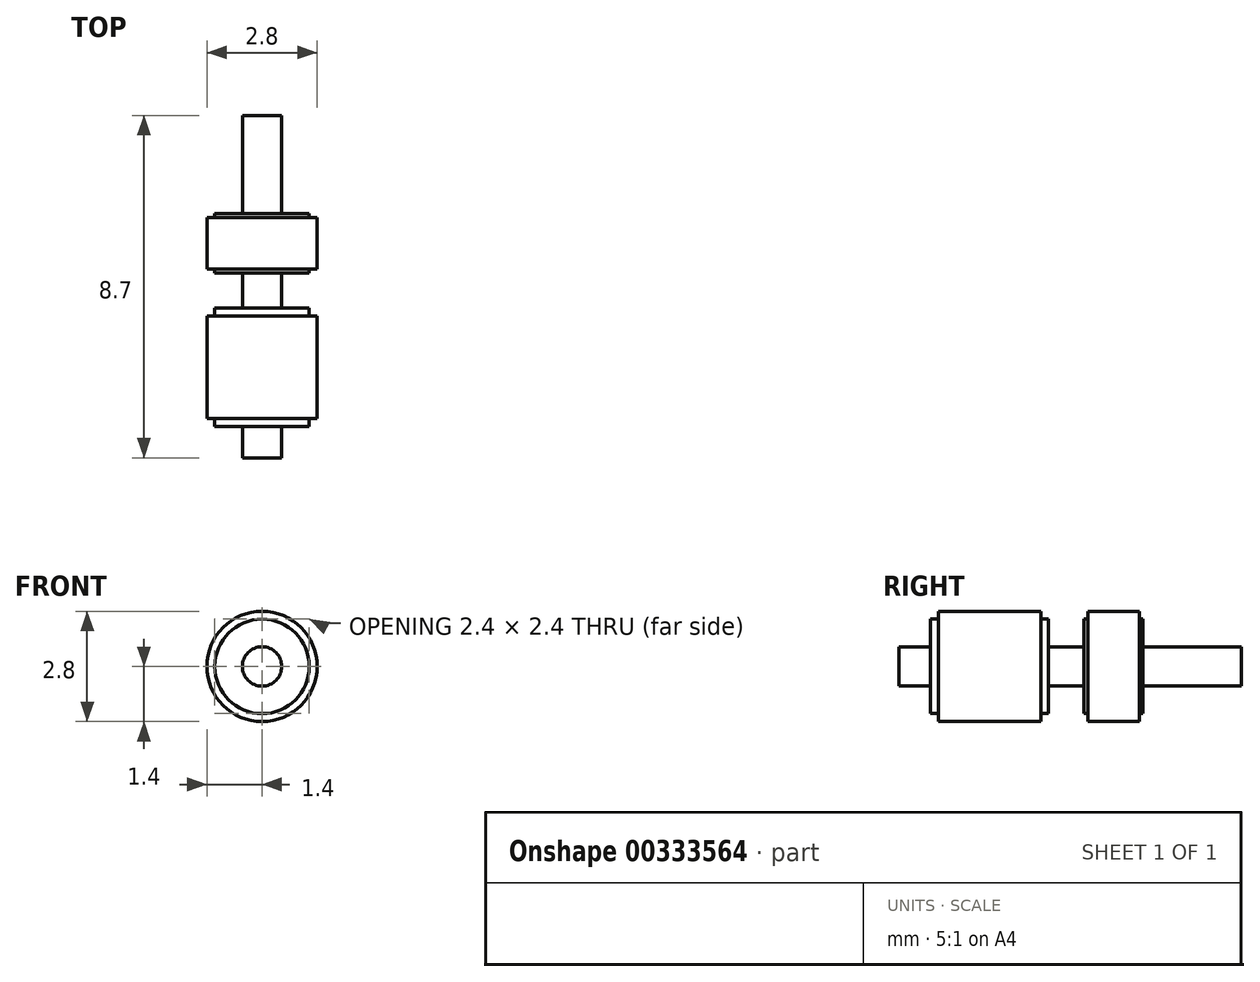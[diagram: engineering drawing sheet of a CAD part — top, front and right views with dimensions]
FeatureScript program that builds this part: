
annotation { "Feature Type Name" : "Feature", "Feature Type Description" : "" }
export const myFeature = defineFeature(function(context is Context, id is Id, definition is map)
    precondition{}
    {
        {
            var Q0;
            Q0=qCreatedBy(makeId("Right.planeOp"),FACE);
            var sketch = newSketch(context, id + "F0", { "sketchPlane" : qUnion([Q0])});
            skLineSegment(sketch, "E0", {"start": v(-0.8, 0) * mm, "end": v(-0.8, 0.5) * mm});
            skLineSegment(sketch, "E1", {"start": v(-0.8, 0.5) * mm, "end": v(0, 0.5) * mm});
            skLineSegment(sketch, "E2", {"start": v(0, 0.5) * mm, "end": v(0, 1.4) * mm});
            skLineSegment(sketch, "E3", {"start": v(0, 1.4) * mm, "end": v(3, 1.4) * mm});
            skLineSegment(sketch, "E4", {"start": v(3, 1.4) * mm, "end": v(3, 0.5) * mm});
            skLineSegment(sketch, "E5", {"start": v(3, 0.5) * mm, "end": v(3.9, 0.5) * mm});
            skLineSegment(sketch, "E6", {"start": v(3.9, 0.5) * mm, "end": v(3.9, 1.2) * mm});
            skLineSegment(sketch, "E7", {"start": v(3.9, 1.2) * mm, "end": v(5.4, 1.2) * mm});
            skLineSegment(sketch, "E8", {"start": v(5.4, 1.2) * mm, "end": v(5.4, 0.5) * mm});
            skLineSegment(sketch, "E9", {"start": v(5.4, 0.5) * mm, "end": v(7.9, 0.5) * mm});
            skLineSegment(sketch, "E10", {"start": v(7.9, 0.5) * mm, "end": v(7.9, 0) * mm});
            skLineSegment(sketch, "E11", {"start": v(7.9, 0) * mm, "end": v(-0.8, 0) * mm});
            skSolve(sketch);
        }
        {
            var Q0;
            Q0=qSketchRegion(id+"F0",true);
            var Q1;
            Q1=sQuery(id+"F0.wireOp",EDGE,"E11");
            revolve(context, id + "F1", {"entities" : qUnion([Q0]), "axis" : qUnion([Q1]), "revolveType" : RevolveType.FULL});
        }
        {
            var Q0;
            Q0=qCreatedBy(makeId("Right.planeOp"),FACE);
            var sketch = newSketch(context, id + "F2", { "sketchPlane" : qUnion([Q0])});
            skLineSegment(sketch, "E12.bottom", {"start": v(0, 1.4) * mm, "end": v(0.2, 1.4) * mm});
            skLineSegment(sketch, "E12.top", {"start": v(0, 1.2) * mm, "end": v(0.2, 1.2) * mm});
            skLineSegment(sketch, "E12.left", {"start": v(0, 1.4) * mm, "end": v(0, 1.2) * mm});
            skLineSegment(sketch, "E12.right", {"start": v(0.2, 1.4) * mm, "end": v(0.2, 1.2) * mm});
            skLineSegment(sketch, "E13.bottom", {"start": v(3, 1.4) * mm, "end": v(2.8, 1.4) * mm});
            skLineSegment(sketch, "E13.top", {"start": v(3, 1.2) * mm, "end": v(2.8, 1.2) * mm});
            skLineSegment(sketch, "E13.left", {"start": v(3, 1.4) * mm, "end": v(3, 1.2) * mm});
            skLineSegment(sketch, "E13.right", {"start": v(2.8, 1.4) * mm, "end": v(2.8, 1.2) * mm});
            skLineSegment(sketch, "E14", {"start": v(0, 1.4) * mm, "end": v(3, 1.4) * mm});
            skLineSegment(sketch, "E15", {"start": v(0, 0) * mm, "end": v(3, 0) * mm, "construction": true});
            skSolve(sketch);
        }
        {
            var Q0;
            Q0 = qSketchRegion(id + "F2", true);
            var Q1;
            Q1=sQuery(id+"F2.wireOp",EDGE,"E15");
            revolve(context, id + "F3", {"operationType" : NewBodyOperationType.REMOVE, "surfaceOperationType" : NewSurfaceOperationType.NEW, "entities" : qUnion([Q0]), "axis" : qUnion([Q1]), "revolveType" : RevolveType.FULL, "oppositeDirection" : true});
        }
        {
            var Q0;
            Q0=qCreatedBy(makeId("Right.planeOp"),FACE);
            var sketch = newSketch(context, id + "F4", { "sketchPlane" : qUnion([Q0])});
            skLineSegment(sketch, "E16.0", {"start": v(5.4, 1.2) * mm, "end": v(5.4, -1.2) * mm});
            skLineSegment(sketch, "E17.0", {"start": v(3.9, 1.2) * mm, "end": v(3.9, -1.2) * mm});
            skLineSegment(sketch, "E18", {"start": v(3.9, 1.2) * mm, "end": v(4.9, 1.2) * mm});
            skLineSegment(sketch, "E19.bottom", {"start": v(4, 1.2) * mm, "end": v(5.3, 1.2) * mm});
            skLineSegment(sketch, "E19.top", {"start": v(4, 1.4) * mm, "end": v(5.3, 1.4) * mm});
            skLineSegment(sketch, "E19.left", {"start": v(4, 1.2) * mm, "end": v(4, 1.4) * mm});
            skLineSegment(sketch, "E19.right", {"start": v(5.3, 1.2) * mm, "end": v(5.3, 1.4) * mm});
            skLineSegment(sketch, "E20", {"start": v(3.9, 0) * mm, "end": v(5.4, 0) * mm, "construction": true});
            skSolve(sketch);
        }
        {
            var Q0;
            Q0 = qSketchRegion(id + "F4", true);
            var Q1;
            Q1=sQuery(id+"F4.wireOp",EDGE,"E20");
            revolve(context, id + "F5", {"operationType" : NewBodyOperationType.ADD, "surfaceOperationType" : NewSurfaceOperationType.NEW, "entities" : qUnion([Q0]), "axis" : qUnion([Q1]), "revolveType" : RevolveType.FULL});
        }
    });
